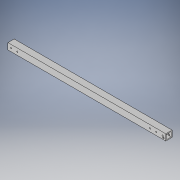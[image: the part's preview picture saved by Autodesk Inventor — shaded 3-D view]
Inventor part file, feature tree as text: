
AUTODESK INVENTOR PART (.ipt)
format: ipt  version: 2018 (Build 220112000, 112)  size: 136,192 bytes
history: native  units: in
note: dims shown in document units (in); Inventor stores cm internally (conversion verified against a paired STEP export)
features: extrude x3, sketch x3
ambient origin geometry x8: Origin, YZ Plane, XZ Plane, XY Plane, X Axis, Y Axis, Z Axis, Center Point
bodies: Solid1 (feature_tree)
feature tree (6):
  extrude  "Extrusion1"  Depth=1.0in
  extrude  "Extrusion3"  Depth=25.0in TaperAngle=0.0deg
  extrude  "Extrusion4"  Depth=1.0in
  sketch  "Sketch1"  dims[d0=1.0in d1=1.0in]
  sketch  "Sketch3"  dims[d2=0.125in d3=25.0in d4=0.0in]
  sketch  "Sketch4"  dims[d7=0.5in d8=1.0in d9=0.5in d10=1.0in d11=0.2031in d12=0.2031in d13=0.2031in d14=0.2031in d15=23.0in d16=0.0in d17=1.0in d18=0.2031in d19=0.256in d20=24.618in d21=0.26in d22=1.0in d23=0.0in]
